# Revit family: Furniture-Mirror-KOHLER-Landshapes-K-32320
name_source: partatom
category: Specialty Equipment
units: mm (PartAtom-declared; Revit-internal decimal feet)

## family parameters
Cut with Voids When Loaded = No
Host = Face
OmniClass Number = 23.21.37.13.15
OmniClass Title = Mirrors
Part Type = Normal
Room Calculation Point = No
Round Connector Dimension = Use Diameter
Shared = No

## types (1)
- STH-Natural Wood
    ADA Compliant = No
    Assembly Code = C1030200
    Date Modified = 04/13/2024
    Default Elevation = 60"
    Description = MIRROR 60 X 38
    Finish = Kohler-Wood-STH-Natural_Wood
    Height = 59 3/4"
    Length = 2 1/4"
    Manufacturer = Kohler Co.
    Master Format 2014 = 06 41 93
    Master Format 2014 Name = Cabinet and Drawer Hardware
    Material = Premium Metal Construction
    Model = K-32320-STH
    Product Documentation Link = https://www.us.kohler.com
    Product Name = Landshapes
    Product Page URL = http://www.us.kohler.com
    Type = 1
    URL = https://www.us.kohler.com
    WaterSense Certified = No
    Width = 38"

## geometry (parser evidence)
native form markers: Sweep x4
no freeform markers — native parametric forms only
